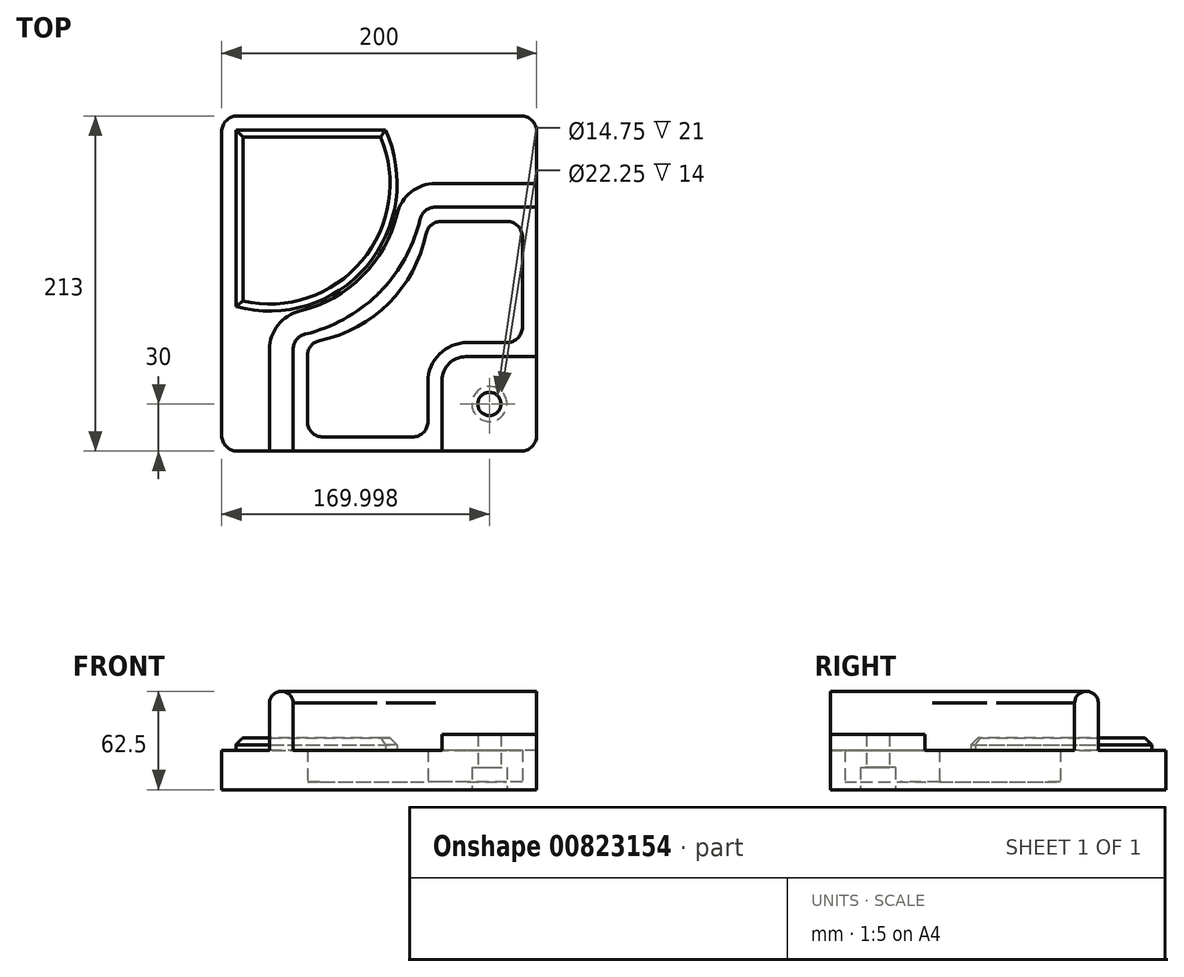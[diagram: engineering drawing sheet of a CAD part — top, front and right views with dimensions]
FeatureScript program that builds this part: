
annotation { "Feature Type Name" : "Feature", "Feature Type Description" : "" }
export const myFeature = defineFeature(function(context is Context, id is Id, definition is map)
    precondition{}
    {
        {
            var Q0;
            Q0=qCreatedBy(makeId("Top.planeOp"),FACE);
            var sketch = newSketch(context, id + "F0", { "sketchPlane" : qUnion([Q0])});
            skLineSegment(sketch, "E0.bottom", {"start": v(-103.25, 124.06) * mm, "end": v(76.75, 124.06) * mm});
            skLineSegment(sketch, "E0.top", {"start": v(-103.25, -88.94) * mm, "end": v(76.75, -88.94) * mm});
            skLineSegment(sketch, "E0.left", {"start": v(-113.25, 114.06) * mm, "end": v(-113.25, -78.94) * mm});
            skLineSegment(sketch, "E0.right", {"start": v(86.75, 114.06) * mm, "end": v(86.75, -78.94) * mm});
            skPoint(sketch, "E0.middle", {"position": v(-13.25, 17.56) * mm});
            skLineSegment(sketch, "E1", {"start": v(86.75, -28.94) * mm, "end": v(41.75, -28.94) * mm});
            skLineSegment(sketch, "E2", {"start": v(26.75, -43.94) * mm, "end": v(26.75, -88.94) * mm});
            skLineSegment(sketch, "E3", {"start": v(86.75, 81.06) * mm, "end": v(22.48, 81.06) * mm});
            skLineSegment(sketch, "E4", {"start": v(-82.88, -24.3) * mm, "end": v(-82.88, -88.94) * mm});
            skPoint(sketch, "E5.visualSharp", {"position": v(26.75, -28.94) * mm});
            skArc(sketch, "E5.filletArc", {"start": v(41.75, -28.94) * mm, "mid": v(31.14, -33.33) * mm, "end": v(26.75, -43.94) * mm});
            skLineSegment(sketch, "E6", {"start": v(17.75, -69.94) * mm, "end": v(17.75, -44.94) * mm});
            skLineSegment(sketch, "E7", {"start": v(42.75, -19.94) * mm, "end": v(67.75, -19.94) * mm});
            skLineSegment(sketch, "E8", {"start": v(-58.88, -69.94) * mm, "end": v(-58.88, -28.44) * mm});
            skLineSegment(sketch, "E9", {"start": v(-48.88, -79.94) * mm, "end": v(7.75, -79.94) * mm});
            skPoint(sketch, "E10.orphan", {"position": v(17.75, -88.94) * mm});
            skPoint(sketch, "E11.orphan", {"position": v(-58.88, -88.94) * mm});
            skLineSegment(sketch, "E12", {"start": v(77.75, -9.94) * mm, "end": v(77.75, 47.06) * mm});
            skPoint(sketch, "E13.orphan", {"position": v(86.75, -19.94) * mm});
            skLineSegment(sketch, "E14", {"start": v(67.75, 57.06) * mm, "end": v(26.3, 57.06) * mm});
            skPoint(sketch, "E15.visualSharp", {"position": v(-58.88, -79.94) * mm});
            skArc(sketch, "E15.filletArc", {"start": v(-58.88, -69.94) * mm, "mid": v(-55.95, -77.01) * mm, "end": v(-48.88, -79.94) * mm});
            skPoint(sketch, "E16.visualSharp", {"position": v(17.75, -79.94) * mm});
            skArc(sketch, "E16.filletArc", {"start": v(7.75, -79.94) * mm, "mid": v(14.82, -77.01) * mm, "end": v(17.75, -69.94) * mm});
            skPoint(sketch, "E17.visualSharp", {"position": v(77.75, -19.94) * mm});
            skArc(sketch, "E17.filletArc", {"start": v(67.75, -19.94) * mm, "mid": v(74.82, -17.01) * mm, "end": v(77.75, -9.94) * mm});
            skPoint(sketch, "E18.visualSharp", {"position": v(77.75, 57.06) * mm});
            skArc(sketch, "E18.filletArc", {"start": v(77.75, 47.06) * mm, "mid": v(74.82, 54.13) * mm, "end": v(67.75, 57.06) * mm});
            skPoint(sketch, "E19.visualSharp", {"position": v(17.75, -19.94) * mm});
            skArc(sketch, "E19.filletArc", {"start": v(42.75, -19.94) * mm, "mid": v(25.07, -27.26) * mm, "end": v(17.75, -44.94) * mm});
            skArc(sketch, "E20", {"start": v(-50.93, -18.66) * mm, "mid": v(-7.1, 5.13) * mm, "end": v(16.5, 49.07) * mm});
            skPoint(sketch, "E21.visualSharp", {"position": v(-58.88, -19.94) * mm});
            skArc(sketch, "E21.filletArc", {"start": v(-50.93, -18.66) * mm, "mid": v(-56.64, -22.14) * mm, "end": v(-58.88, -28.44) * mm});
            skPoint(sketch, "E22.visualSharp", {"position": v(17.75, 57.06) * mm});
            skArc(sketch, "E22.filletArc", {"start": v(26.3, 57.06) * mm, "mid": v(19.97, 54.8) * mm, "end": v(16.5, 49.07) * mm});
            skPoint(sketch, "E23.visualSharp", {"position": v(86.75, 124.06) * mm});
            skArc(sketch, "E23.filletArc", {"start": v(86.75, 114.06) * mm, "mid": v(83.82, 121.13) * mm, "end": v(76.75, 124.06) * mm});
            skPoint(sketch, "E24.visualSharp", {"position": v(-113.25, 124.06) * mm});
            skArc(sketch, "E24.filletArc", {"start": v(-103.25, 124.06) * mm, "mid": v(-110.32, 121.13) * mm, "end": v(-113.25, 114.06) * mm});
            skPoint(sketch, "E25.visualSharp", {"position": v(-113.25, -88.94) * mm});
            skArc(sketch, "E25.filletArc", {"start": v(-113.25, -78.94) * mm, "mid": v(-110.32, -86.01) * mm, "end": v(-103.25, -88.94) * mm});
            skPoint(sketch, "E26.visualSharp", {"position": v(86.75, -88.94) * mm});
            skArc(sketch, "E26.filletArc", {"start": v(76.75, -88.94) * mm, "mid": v(83.82, -86.01) * mm, "end": v(86.75, -78.94) * mm});
            skLineSegment(sketch, "E27", {"start": v(-67.88, -88.94) * mm, "end": v(-67.88, -23.74) * mm});
            skLineSegment(sketch, "E28", {"start": v(86.75, 66.06) * mm, "end": v(22, 66.06) * mm});
            skArc(sketch, "E29", {"start": v(-63.65, 0.03) * mm, "mid": v(-23.98, 22.17) * mm, "end": v(-1.84, 61.83) * mm});
            skArc(sketch, "E30.filletArc", {"start": v(-63.65, 0.03) * mm, "mid": v(-77.49, -8.8) * mm, "end": v(-82.88, -24.3) * mm});
            skPoint(sketch, "E31.visualSharp", {"position": v(0.4, 81.06) * mm});
            skArc(sketch, "E31.filletArc", {"start": v(22.48, 81.06) * mm, "mid": v(6.98, 75.67) * mm, "end": v(-1.84, 61.83) * mm});
            skArc(sketch, "E32", {"start": v(-104.25, 2.93) * mm, "mid": v(-21.05, 28.73) * mm, "end": v(-9.36, 115.06) * mm});
            skLineSegment(sketch, "E33", {"start": v(-104.25, 115.06) * mm, "end": v(-104.25, 2.93) * mm});
            skLineSegment(sketch, "E34", {"start": v(-104.25, 115.06) * mm, "end": v(-9.36, 115.06) * mm});
            skPoint(sketch, "E35.orphan", {"position": v(17.75, 66.06) * mm});
            skPoint(sketch, "E36.visualSharp", {"position": v(-67.88, -15.36) * mm});
            skPoint(sketch, "E37.visualSharp", {"position": v(10.26, 66.06) * mm});
            skArc(sketch, "E38", {"start": v(-60.03, -13.97) * mm, "mid": v(-13.36, 11.58) * mm, "end": v(12.25, 58.22) * mm});
            skArc(sketch, "E39.filletArc", {"start": v(-60.03, -13.97) * mm, "mid": v(-65.67, -17.47) * mm, "end": v(-67.88, -23.74) * mm});
            skPoint(sketch, "E40.visualSharp", {"position": v(13.64, 66.06) * mm});
            skArc(sketch, "E40.filletArc", {"start": v(22, 66.06) * mm, "mid": v(15.75, 63.86) * mm, "end": v(12.25, 58.22) * mm});
            skLineSegment(sketch, "E41", {"start": v(56.75, -88.94) * mm, "end": v(56.75, -28.94) * mm, "construction": true});
            skLineSegment(sketch, "E42", {"start": v(26.75, -58.94) * mm, "end": v(86.75, -58.94) * mm, "construction": true});
            skPoint(sketch, "E43", {"position": v(56.75, -58.94) * mm});
            skSolve(sketch);
        }
        {
            var Q0;
            {var subQ1=sQuery(id+"F0.wireOp",EDGE,"E1");Q0=makeQuery(id+"F0.imprint","IMPRINT",FACE,{"disambiguationData":[TD([[makeQuery(id+"F0.imprint","IMPRINT",EDGE,{"derivedFrom":subQ1}),1.0]])]});}
            extrude(context, id + "F1", {"entities" : qUnion([Q0]), "depth" : 35 * mm, "offsetDistance" : 25.4 * mm});
        }
        {
            var Q0;
            {var subQ3=sQuery(id+"F0.wireOp",EDGE,"E1");Q0=makeQuery(id+"F0.imprint","IMPRINT",FACE,{"disambiguationData":[TD([[makeQuery(id+"F0.imprint","IMPRINT",EDGE,{"derivedFrom":subQ3}),-1.0]])]});}
            extrude(context, id + "F2", {"entities" : qUnion([Q0]), "operationType" : NewBodyOperationType.ADD, "depth" : 25 * mm, "offsetDistance" : 25.4 * mm});
        }
        {
            var Q0;
            {var subQ2=sQuery(id+"F0.wireOp",EDGE,"E3");Q0=makeQuery(id+"F0.imprint","IMPRINT",FACE,{"disambiguationData":[TD([[makeQuery(id+"F0.imprint","IMPRINT",EDGE,{"derivedFrom":subQ2}),1.0]])]});}
            extrude(context, id + "F3", {"entities" : qUnion([Q0]), "operationType" : NewBodyOperationType.ADD, "depth" : 55 * mm, "offsetDistance" : 25 * mm});
        }
        {
            var Q0;
            Q0=makeQuery(id+"F0.imprint","IMPRINT",FACE,{"disambiguationData":[TD([[makeQuery(id+"F0.imprint","IMPRINT",EDGE,{"derivedFrom":sQuery(id+"F0.wireOp",EDGE,"E0.bottom")}),-1.0]])]});
            extrude(context, id + "F4", {"entities" : qUnion([Q0]), "operationType" : NewBodyOperationType.ADD, "depth" : 25 * mm, "offsetDistance" : 25 * mm});
        }
        {
            var Q0;
            Q0=makeQuery(id+"F0.imprint","IMPRINT",FACE,{"disambiguationData":[TD([[makeQuery(id+"F0.imprint","IMPRINT",EDGE,{"derivedFrom":sQuery(id+"F0.wireOp",EDGE,"E32")}),1.0]])]});
            extrude(context, id + "F5", {"entities" : qUnion([Q0]), "operationType" : NewBodyOperationType.ADD, "depth" : 33 * mm, "offsetDistance" : 25 * mm});
        }
        {
            var Q0;
            Q0=makeQuery(id+"F0.imprint","IMPRINT",FACE,{"disambiguationData":[TD([[makeQuery(id+"F0.imprint","IMPRINT",EDGE,{"derivedFrom":sQuery(id+"F0.wireOp",EDGE,"E6")}),1.0]])]});
            extrude(context, id + "F6", {"entities" : qUnion([Q0]), "operationType" : NewBodyOperationType.ADD, "depth" : 5 * mm, "offsetDistance" : 25 * mm});
        }
        {
            var Q0;
            {var subQ0=sQuery(id+"F0.wireOp",EDGE,"E0.top");Q0=makeQuery(id+"F4.boolean.opBoolean","MERGE",FACE,{"derivedFrom":[makeQuery(id+"F3.boolean.opBoolean","MERGE",FACE,{"derivedFrom":[makeQuery(id+"F2.boolean.opBoolean","MERGE",FACE,{"derivedFrom":[makeQuery(id+"F1.opExtrude","SWEPT_FACE",FACE,{"disambiguationData":[OSD([subQ0])]}),makeQuery(id+"F2.opExtrude","SWEPT_FACE",FACE,{"disambiguationData":[OSD([subQ0])]})]}),makeQuery(id+"F3.opExtrude","SWEPT_FACE",FACE,{"disambiguationData":[OSD([subQ0])]})]}),makeQuery(id+"F4.opExtrude","SWEPT_FACE",FACE,{"disambiguationData":[OSD([subQ0])]})]});}
            var sketch = newSketch(context, id + "F7", { "sketchPlane" : qUnion([Q0])});
            skLineSegment(sketch, "E44.0", {"start": v(-82.88, 55) * mm, "end": v(-82.88, 25) * mm});
            skLineSegment(sketch, "E45.0", {"start": v(-67.88, 55) * mm, "end": v(-67.88, 25) * mm});
            skLineSegment(sketch, "E46.0", {"start": v(-82.88, 55) * mm, "end": v(-67.88, 55) * mm});
            skArc(sketch, "E47", {"start": v(-67.88, 55) * mm, "mid": v(-75.38, 62.5) * mm, "end": v(-82.88, 55) * mm});
            skSolve(sketch);
        }
        {
            var Q0;
            Q0=makeQuery(id+"F7.imprint","IMPRINT",FACE,{"disambiguationData":[TD([[makeQuery(id+"F7.imprint","IMPRINT",EDGE,{"derivedFrom":sQuery(id+"F7.wireOp",EDGE,"E46.0")}),1.0]])]});
            var Q1;
            Q1=makeQuery(id+"F3.opExtrude","CAP_EDGE",EDGE,{"disambiguationData":[OSD([sQuery(id+"F0.wireOp",EDGE,"E4")])],"isStart":false});
            var Q2;
            Q2=makeQuery(id+"F3.opExtrude","CAP_EDGE",EDGE,{"disambiguationData":[OSD([sQuery(id+"F0.wireOp",EDGE,"E30.filletArc")])],"isStart":false});
            var Q3;
            Q3=makeQuery(id+"F3.opExtrude","CAP_EDGE",EDGE,{"disambiguationData":[OSD([sQuery(id+"F0.wireOp",EDGE,"E29")])],"isStart":false});
            var Q4;
            Q4=makeQuery(id+"F3.opExtrude","CAP_EDGE",EDGE,{"disambiguationData":[OSD([sQuery(id+"F0.wireOp",EDGE,"E31.filletArc")])],"isStart":false});
            var Q5;
            Q5=makeQuery(id+"F3.opExtrude","CAP_EDGE",EDGE,{"disambiguationData":[OSD([sQuery(id+"F0.wireOp",EDGE,"E3")])],"isStart":false});
            sweep(context, id + "F8", {"operationType" : NewBodyOperationType.ADD, "profiles" : qUnion([Q0]), "path" : qUnion([Q1, Q2, Q3, Q4, Q5])});
        }
        {
            var Q0;
            Q0=makeQuery(id+"F5.opExtrude","CAP_EDGE",EDGE,{"disambiguationData":[OSD([sQuery(id+"F0.wireOp",EDGE,"E34")])],"isStart":false});
            var Q1;
            Q1=makeQuery(id+"F5.opExtrude","CAP_EDGE",EDGE,{"disambiguationData":[OSD([sQuery(id+"F0.wireOp",EDGE,"E32")])],"isStart":false});
            var Q2;
            Q2=makeQuery(id+"F5.opExtrude","CAP_EDGE",EDGE,{"disambiguationData":[OSD([sQuery(id+"F0.wireOp",EDGE,"E33")])],"isStart":false});
            chamfer(context, id + "F9", {"entities" : qUnion([Q0, Q1, Q2]), "width" : 4.5 * mm, "tangentPropagation" : true});
        }
        {
            var Q0;
            Q0=sQuery(id+"F0.wireOp",VERTEX,"E43");
            var Q1;
            Q1=makeQuery(id+"F1.opExtrude","SWEPT_BODY",BODY,{"disambiguationData":[OSD([sQuery(id+"F0.wireOp",EDGE,"E0.top"),sQuery(id+"F0.wireOp",EDGE,"E0.right"),sQuery(id+"F0.wireOp",EDGE,"E1"),sQuery(id+"F0.wireOp",EDGE,"E2"),sQuery(id+"F0.wireOp",EDGE,"E5.filletArc"),sQuery(id+"F0.wireOp",EDGE,"E26.filletArc")])]});
            hole(context, id + "F10", {"style" : HoleStyle.C_BORE, "endStyle" : HoleEndStyle.THROUGH, "oppositeDirection" : true, "standardTappedOrClearance" : lookupTablePath({ "standard" : "ISO", "fit" : "Close", "size" : "M14", "type" : "Clearance" }), "standardBlindInLast" : lookupTablePath({ "fit" : "Close", "standard" : "ISO", "size" : "M14", "type" : "Clearance" }), "holeDiameter" : 14.75 * mm, "cBoreDiameter" : 22.25 * mm, "cBoreDepth" : 14 * mm, "majorDiameter" : 5 * mm, "isTappedThrough" : true, "tappedDepth" : 12 * mm, "tapClearance" : 3, "locations" : qUnion([Q0]), "scope" : qUnion([Q1])});
        }
    });
